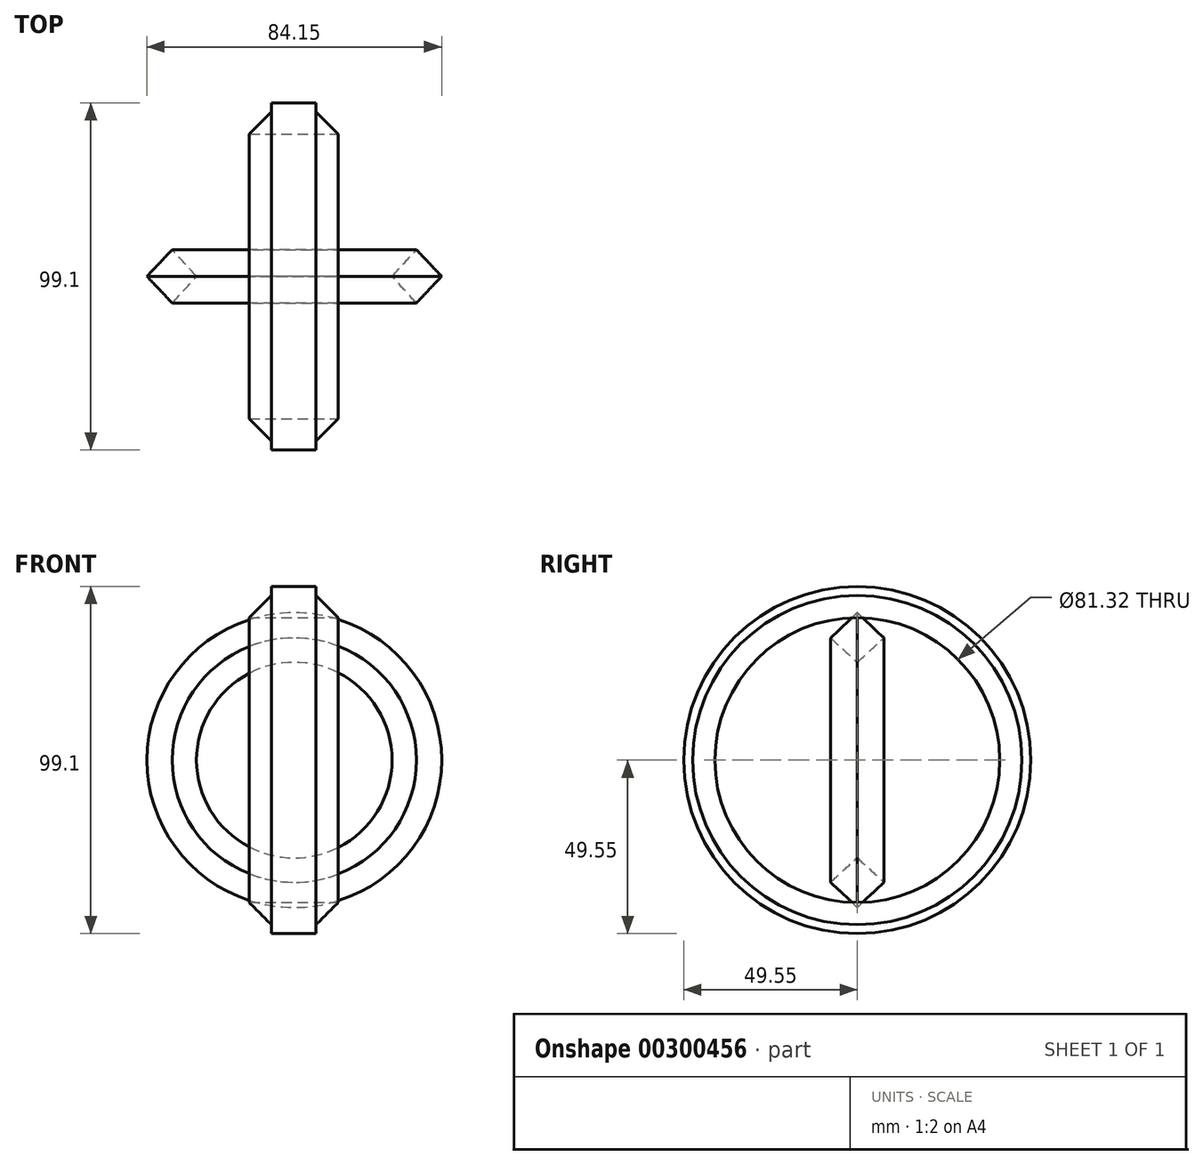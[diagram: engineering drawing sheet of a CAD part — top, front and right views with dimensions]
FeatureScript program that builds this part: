
annotation { "Feature Type Name" : "Feature", "Feature Type Description" : "" }
export const myFeature = defineFeature(function(context is Context, id is Id, definition is map)
    precondition{}
    {
        {
            var Q0;
            Q0=qCreatedBy(makeId("Front.planeOp"),FACE);
            var sketch = newSketch(context, id + "F0", { "sketchPlane" : qUnion([Q0])});
            skLineSegment(sketch, "E0", {"start": v(0, -40.66) * mm, "end": v(-25.4, -40.66) * mm});
            skLineSegment(sketch, "E1", {"start": v(-19.05, -47.01) * mm, "end": v(-19.05, -49.55) * mm});
            skLineSegment(sketch, "E2", {"start": v(-19.05, -49.55) * mm, "end": v(-6.35, -49.55) * mm});
            skLineSegment(sketch, "E3", {"start": v(-6.35, -49.55) * mm, "end": v(-6.35, -47.01) * mm});
            skLineSegment(sketch, "E4", {"start": v(-25.4, -40.66) * mm, "end": v(-19.05, -47.01) * mm});
            skLineSegment(sketch, "E5", {"start": v(-6.35, -47.01) * mm, "end": v(0, -40.66) * mm});
            skSolve(sketch);
        }
        {
            var Q0;
            Q0=qCreatedBy(makeId("Right.planeOp"),FACE);
            var sketch = newSketch(context, id + "F1", { "sketchPlane" : qUnion([Q0])});
            skCircle(sketch, "E6", {"center": v(0, 0) * mm, "radius": 44.45 * mm});
            skSolve(sketch);
        }
        {
            var Q0;
            Q0=makeQuery(id+"F0.imprint","IMPRINT",FACE,{"disambiguationData":[TD([[makeQuery(id+"F0.imprint","IMPRINT",EDGE,{"derivedFrom":sQuery(id+"F0.wireOp",EDGE,"E0")}),1.0]])]});
            var Q1;
            Q1=sQuery(id+"F1.wireOp",EDGE,"E6");
            sweep(context, id + "F2", {"profiles" : qUnion([Q0]), "path" : qUnion([Q1])});
        }
        {
            var Q0;
            Q0=qCreatedBy(makeId("Front.planeOp"),FACE);
            var sketch = newSketch(context, id + "F3", { "sketchPlane" : qUnion([Q0])});
            skCircle(sketch, "E7", {"center": v(-12.54, 0) * mm, "radius": 38.1 * mm});
            skSolve(sketch);
        }
        {
            var Q0;
            Q0=qCreatedBy(makeId("Right.planeOp"),FACE);
            var sketch = newSketch(context, id + "F4", { "sketchPlane" : qUnion([Q0])});
            skLineSegment(sketch, "E8", {"start": v(0, -40.17) * mm, "end": v(7.6, -32.57) * mm});
            skLineSegment(sketch, "E9", {"start": v(7.6, -32.57) * mm, "end": v(-0.02, -24.95) * mm});
            skLineSegment(sketch, "E10", {"start": v(-0.02, -24.95) * mm, "end": v(-7.62, -32.55) * mm});
            skLineSegment(sketch, "E11", {"start": v(-7.62, -32.55) * mm, "end": v(0, -40.17) * mm});
            skSolve(sketch);
        }
        {
            var Q0;
            Q0=makeQuery(id+"F4.imprint","IMPRINT",FACE,{"disambiguationData":[TD([[makeQuery(id+"F4.imprint","IMPRINT",EDGE,{"derivedFrom":sQuery(id+"F4.wireOp",EDGE,"E8")}),1.0]])]});
            var Q1;
            Q1=sQuery(id+"F3.wireOp",EDGE,"E7");
            sweep(context, id + "F5", {"profiles" : qUnion([Q0]), "path" : qUnion([Q1])});
        }
    });
